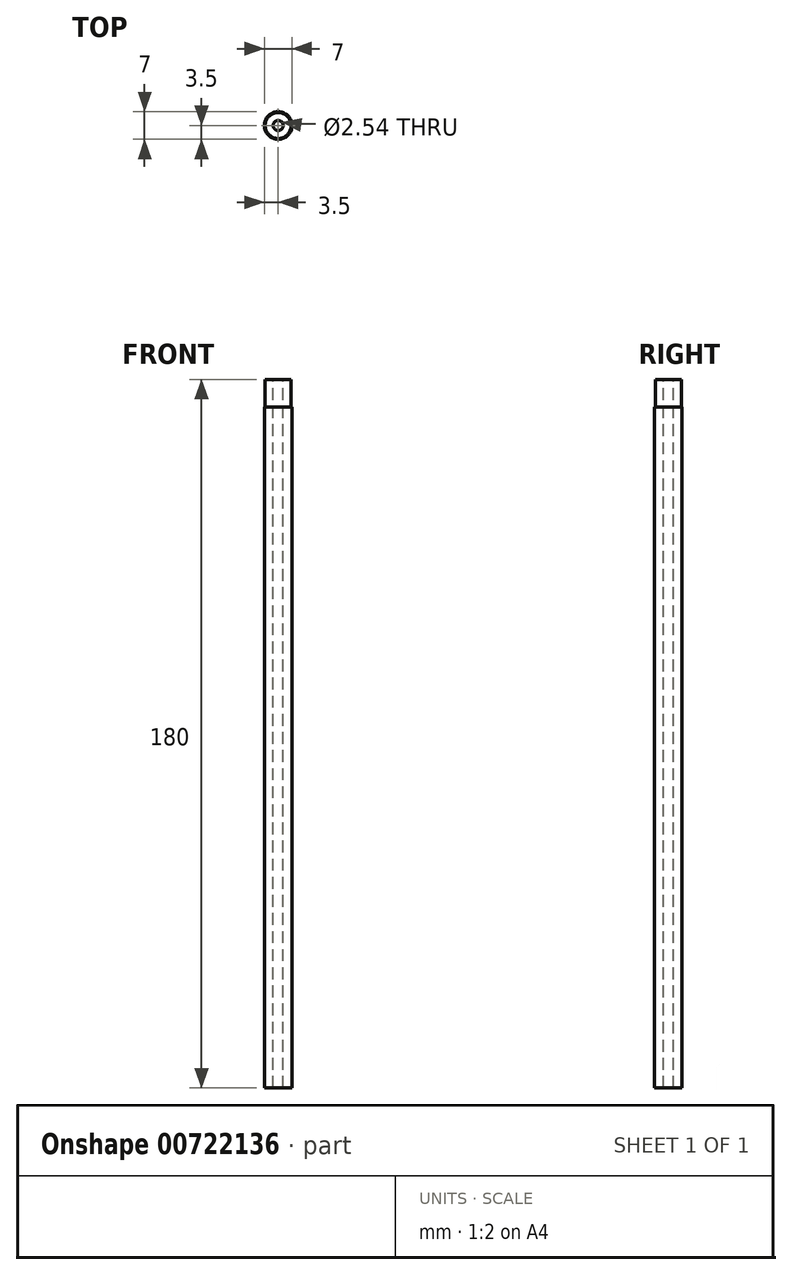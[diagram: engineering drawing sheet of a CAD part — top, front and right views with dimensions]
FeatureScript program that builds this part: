
annotation { "Feature Type Name" : "Feature", "Feature Type Description" : "" }
export const myFeature = defineFeature(function(context is Context, id is Id, definition is map)
    precondition{}
    {
        {
            var Q0;
            Q0=qCreatedBy(makeId("Front.planeOp"),FACE);
            var sketch = newSketch(context, id + "F0", { "sketchPlane" : qUnion([Q0])});
            skLineSegment(sketch, "E0", {"start": v(0, 105) * mm, "end": v(0, -105) * mm});
            skLineSegment(sketch, "E1", {"start": v(-70, 0) * mm, "end": v(70, 0) * mm});
            skLineSegment(sketch, "E2", {"start": v(-3.5, 83) * mm, "end": v(-3.5, -90) * mm});
            skLineSegment(sketch, "E3", {"start": v(-3.5, -90) * mm, "end": v(-1.27, -90) * mm});
            skLineSegment(sketch, "E4", {"start": v(-1.27, 90) * mm, "end": v(-3.3, 90) * mm});
            skLineSegment(sketch, "E5", {"start": v(-1.27, 90) * mm, "end": v(-1.27, -90) * mm});
            skLineSegment(sketch, "E6", {"start": v(-3.3, 83) * mm, "end": v(-3.5, 83) * mm});
            skLineSegment(sketch, "E7", {"start": v(-3.3, 90) * mm, "end": v(-3.3, 83) * mm});
            skSolve(sketch);
        }
        {
            var Q0;
            {var subQ5=sQuery(id+"F0.wireOp",EDGE,"E3");Q0=makeQuery(id+"F0.imprint","IMPRINT",FACE,{"disambiguationData":[TD([[makeQuery(id+"F0.imprint","IMPRINT",EDGE,{"derivedFrom":subQ5}),1.0]])]});}
            var Q1;
            {var subQ0=sQuery(id+"F0.wireOp",EDGE,"E4");Q1=makeQuery(id+"F0.imprint","IMPRINT",FACE,{"disambiguationData":[TD([[makeQuery(id+"F0.imprint","IMPRINT",EDGE,{"derivedFrom":subQ0}),1.0]])]});}
            var Q2;
            Q2=sQuery(id+"F0.wireOp",EDGE,"E0");
            revolve(context, id + "F1", {"surfaceOperationType" : NewSurfaceOperationType.NEW, "entities" : qUnion([Q0, Q1]), "axis" : qUnion([Q2]), "revolveType" : RevolveType.FULL});
        }
    });
